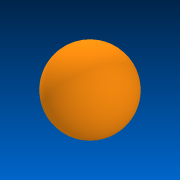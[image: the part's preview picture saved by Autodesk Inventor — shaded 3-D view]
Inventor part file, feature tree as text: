
AUTODESK INVENTOR PART (.ipt)
format: ipt  version: 2022.2 (Build 262287000, 287)  size: 136,192 bytes
history: native  units: in
note: dims shown in document units (in); Inventor stores cm internally (conversion verified against a paired STEP export)
features: revolve x1, shell x1, sketch x1
ambient origin geometry x8: Origin, YZ Plane, XZ Plane, XY Plane, X Axis, Y Axis, Z Axis, Center Point
bodies: Solid1 (feature_tree)
feature tree (3):
  revolve  "Revolution1"  Angle=180.0deg
  shell  "Shell1"  Thickness=0.1in
  sketch  "Sketch1"  dims[d0=9.3901in d1=180.0deg d2=0.1in]
